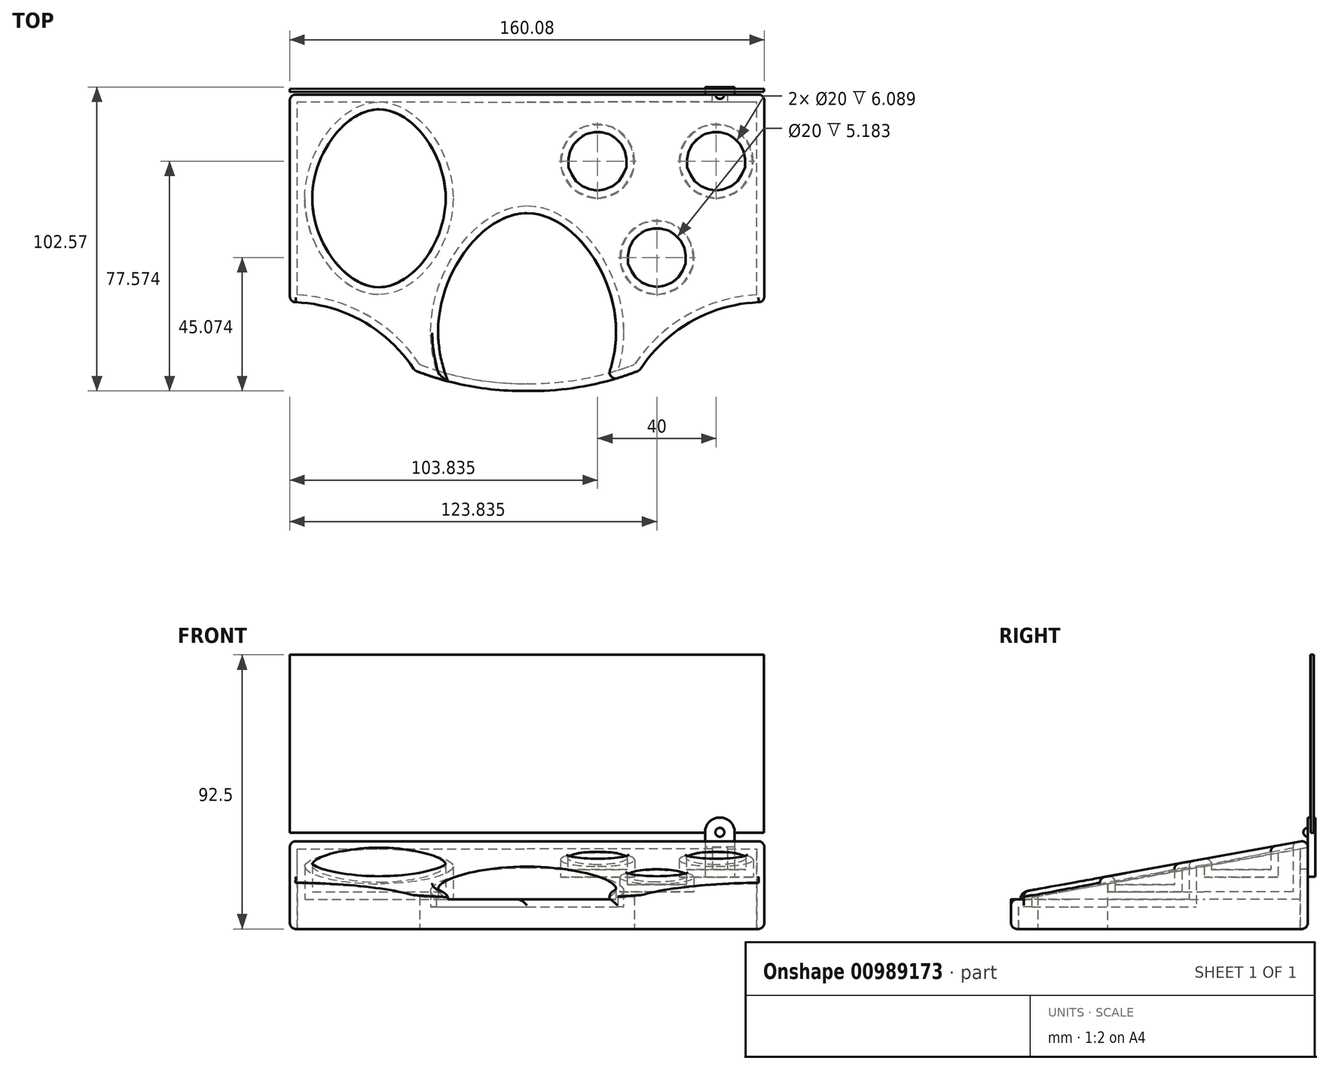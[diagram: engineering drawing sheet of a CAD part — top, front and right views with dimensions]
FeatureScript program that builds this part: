
annotation { "Feature Type Name" : "Feature", "Feature Type Description" : "" }
export const myFeature = defineFeature(function(context is Context, id is Id, definition is map)
    precondition{}
    {
        {
            var Q0;
            Q0=qCreatedBy(makeId("Top.planeOp"),FACE);
            var sketch = newSketch(context, id + "F0", { "sketchPlane" : qUnion([Q0])});
            skLineSegment(sketch, "E0.left", {"start": v(-80, 30) * mm, "end": v(-80, 100.06) * mm});
            skLineSegment(sketch, "E1", {"start": v(0, 0) * mm, "end": v(0, 30) * mm});
            skArc(sketch, "E2", {"start": v(-37.87, 6.93) * mm, "mid": v(-19.27, 1.63) * mm, "end": v(0, 0) * mm});
            skArc(sketch, "E3", {"start": v(-37.87, 6.93) * mm, "mid": v(-55.99, 23.86) * mm, "end": v(-80, 30) * mm});
            skLineSegment(sketch, "E4", {"start": v(0, 0) * mm, "end": v(0, 100) * mm});
            skLineSegment(sketch, "E5", {"start": v(-80, 100.06) * mm, "end": v(0, 100) * mm});
            skLineSegment(sketch, "E6.MirrorCS", {"start": v(80, 100.06) * mm, "end": v(0, 100) * mm});
            skLineSegment(sketch, "E7.MirrorCS", {"start": v(80, 30) * mm, "end": v(80, 100.06) * mm});
            skArc(sketch, "E8.MirrorCS", {"start": v(37.87, 6.93) * mm, "mid": v(55.99, 23.86) * mm, "end": v(80, 30) * mm});
            skArc(sketch, "E9.MirrorCS", {"start": v(37.87, 6.93) * mm, "mid": v(19.27, 1.63) * mm, "end": v(0, 0) * mm});
            skSolve(sketch);
        }
        {
            var Q0;
            Q0=makeQuery(id+"F0.imprint","IMPRINT",FACE,{"disambiguationData":[TD([[makeQuery(id+"F0.imprint","IMPRINT",EDGE,{"derivedFrom":sQuery(id+"F0.wireOp",EDGE,"E0.left")}),-1.0]])]});
            var Q1;
            {var subQ0=sQuery(id+"F0.wireOp",EDGE,"E6.MirrorCS");Q1=makeQuery(id+"F0.imprint","IMPRINT",FACE,{"disambiguationData":[TD([[makeQuery(id+"F0.imprint","IMPRINT",EDGE,{"derivedFrom":subQ0}),1.0]])]});}
            extrude(context, id + "F1", {"entities" : qUnion([Q0, Q1]), "depth" : 30 * mm, "offsetDistance" : 25 * mm});
        }
        {
            var Q0;
            Q0=makeQuery(id+"F1.opExtrude","SWEPT_FACE",FACE,{"disambiguationData":[OSD([sQuery(id+"F0.wireOp",EDGE,"E7.MirrorCS")])]});
            var sketch = newSketch(context, id + "F2", { "sketchPlane" : qUnion([Q0])});
            skLineSegment(sketch, "E10", {"start": v(0, 0) * mm, "end": v(-10, 0) * mm});
            skLineSegment(sketch, "E11", {"start": v(-10, 0) * mm, "end": v(-10, 10) * mm});
            skLineSegment(sketch, "E12", {"start": v(-10, 10) * mm, "end": v(-10, 30) * mm});
            skLineSegment(sketch, "E13", {"start": v(-10, 30) * mm, "end": v(100.06, 30) * mm});
            skLineSegment(sketch, "E14", {"start": v(100.06, 30) * mm, "end": v(-10, 10) * mm});
            skSolve(sketch);
        }
        {
            var Q0;
            Q0 = qSketchRegion(id + "F2", true);
            extrude(context, id + "F3", {"entities" : qUnion([Q0]), "operationType" : NewBodyOperationType.REMOVE, "endBound" : BoundingType.THROUGH_ALL, "oppositeDirection" : true, "depth" : 25 * mm, "offsetDistance" : 25 * mm});
        }
        {
            var Q0;
            Q0=qCreatedBy(makeId("Right.planeOp"),FACE);
            var sketch = newSketch(context, id + "F4", { "sketchPlane" : qUnion([Q0])});
            skLineSegment(sketch, "E15", {"start": v(0, 0) * mm, "end": v(0, 10) * mm});
            skLineSegment(sketch, "E16", {"start": v(0, 10) * mm, "end": v(40, 10) * mm});
            skLineSegment(sketch, "E17", {"start": v(40, 10) * mm, "end": v(40, 30) * mm});
            skLineSegment(sketch, "E18", {"start": v(40, 30) * mm, "end": v(0, 30) * mm});
            skLineSegment(sketch, "E19", {"start": v(0, 30) * mm, "end": v(0, 10) * mm});
            skLineSegment(sketch, "E20", {"start": v(0, 30) * mm, "end": v(-10, 30) * mm});
            skLineSegment(sketch, "E21", {"start": v(-10, 30) * mm, "end": v(-10, 10) * mm});
            skLineSegment(sketch, "E22", {"start": v(-10, 10) * mm, "end": v(0, 10) * mm});
            skSolve(sketch);
        }
        {
            var Q0;
            Q0 = qSketchRegion(id + "F4", true);
            extrude(context, id + "F5", {"entities" : qUnion([Q0]), "operationType" : NewBodyOperationType.REMOVE, "depth" : 10 * mm, "offsetDistance" : 25 * mm, "hasSecondDirection" : true, "secondDirectionOppositeDirection" : true, "secondDirectionDepth" : 10 * mm});
        }
        {
            var Q0;
            Q0=makeQuery(id+"F5.boolean.opBoolean","COPY",FACE,{"derivedFrom":makeQuery(id+"F5.opExtrude","SWEPT_FACE",FACE,{"disambiguationData":[OSD([sQuery(id+"F4.wireOp",EDGE,"E16"),sQuery(id+"F4.wireOp",EDGE,"E22")])]})});
            var sketch = newSketch(context, id + "F6", { "sketchPlane" : qUnion([Q0])});
            skLineSegment(sketch, "E23", {"start": v(0, 0) * mm, "end": v(0, 60) * mm});
            skLineSegment(sketch, "E24", {"start": v(0, 60) * mm, "end": v(0, -20) * mm});
            skLineSegment(sketch, "E25", {"start": v(0, 20) * mm, "end": v(-30, 20) * mm});
            skLineSegment(sketch, "E26", {"start": v(0, 20) * mm, "end": v(30, 20) * mm});
            skFitSpline(sketch, "E27", {"points": [v(-30, 20) * mm, v(0, 60) * mm, v(30, 20) * mm, v(0, -20) * mm, v(-30, 20) * mm]});
            skSolve(sketch);
        }
        {
            var Q0;
            Q0 = qSketchRegion(id + "F6", true);
            extrude(context, id + "F7", {"entities" : qUnion([Q0]), "operationType" : NewBodyOperationType.REMOVE, "endBound" : BoundingType.THROUGH_ALL, "depth" : 25 * mm, "offsetDistance" : 25 * mm});
        }
        {
            var Q0;
            Q0=makeQuery(id+"F7.boolean.opBoolean","MERGE",FACE,{"derivedFrom":[makeQuery(id+"F5.boolean.opBoolean","COPY",FACE,{"derivedFrom":makeQuery(id+"F5.opExtrude","SWEPT_FACE",FACE,{"disambiguationData":[OSD([sQuery(id+"F4.wireOp",EDGE,"E16"),sQuery(id+"F4.wireOp",EDGE,"E22")])]})})],"fromTools":[makeQuery(id+"F7.opExtrude","CAP_FACE",FACE,{"disambiguationData":[OSD([sQuery(id+"F6.wireOp",EDGE,"E27")])],"isStart":true})]});
            var sketch = newSketch(context, id + "F8", { "sketchPlane" : qUnion([Q0])});
            skLineSegment(sketch, "E28", {"start": v(0, 0) * mm, "end": v(1.26, 100.06) * mm});
            skLineSegment(sketch, "E29", {"start": v(1.26, 100.06) * mm, "end": v(81.26, 100.06) * mm});
            skLineSegment(sketch, "E30", {"start": v(41.26, 100.06) * mm, "end": v(43.76, 100.06) * mm});
            skLineSegment(sketch, "E31", {"start": v(43.76, 100.06) * mm, "end": v(43.76, 45.06) * mm});
            skLineSegment(sketch, "E32", {"start": v(43.76, 45.06) * mm, "end": v(43.76, 65.06) * mm});
            skCircle(sketch, "E33", {"center": v(23.76, 77.56) * mm, "radius": 10 * mm});
            skCircle(sketch, "E34", {"center": v(63.76, 77.56) * mm, "radius": 10 * mm});
            skCircle(sketch, "E35", {"center": v(43.76, 45.06) * mm, "radius": 10 * mm});
            skLineSegment(sketch, "E36", {"start": v(63.76, 77.56) * mm, "end": v(23.76, 77.56) * mm});
            skLineSegment(sketch, "E37", {"start": v(43.76, 77.56) * mm, "end": v(43.76, 45.06) * mm});
            skLineSegment(sketch, "E38", {"start": v(63.76, 77.56) * mm, "end": v(43.76, 77.56) * mm});
            skLineSegment(sketch, "E39", {"start": v(23.76, 77.56) * mm, "end": v(43.76, 77.56) * mm});
            skSolve(sketch);
        }
        {
            var Q0;
            Q0 = qSketchRegion(id + "F8", true);
            extrude(context, id + "F9", {"entities" : qUnion([Q0]), "operationType" : NewBodyOperationType.REMOVE, "endBound" : BoundingType.THROUGH_ALL, "depth" : 25 * mm, "offsetDistance" : 25 * mm});
        }
        {
            var Q0;
            Q0=makeQuery(id+"F7.boolean.opBoolean","MERGE",FACE,{"derivedFrom":[makeQuery(id+"F5.boolean.opBoolean","COPY",FACE,{"derivedFrom":makeQuery(id+"F5.opExtrude","SWEPT_FACE",FACE,{"disambiguationData":[OSD([sQuery(id+"F4.wireOp",EDGE,"E16"),sQuery(id+"F4.wireOp",EDGE,"E22")])]})})],"fromTools":[makeQuery(id+"F7.opExtrude","CAP_FACE",FACE,{"disambiguationData":[OSD([sQuery(id+"F6.wireOp",EDGE,"E27")])],"isStart":true})]});
            var sketch = newSketch(context, id + "F10", { "sketchPlane" : qUnion([Q0])});
            skLineSegment(sketch, "E40", {"start": v(-39.95, 100.02) * mm, "end": v(-49.95, 100.02) * mm});
            skLineSegment(sketch, "E41", {"start": v(-49.95, 100.02) * mm, "end": v(-49.95, 65.02) * mm});
            skLineSegment(sketch, "E42", {"start": v(-49.95, 65.02) * mm, "end": v(-49.95, 35.02) * mm});
            skLineSegment(sketch, "E43", {"start": v(-49.95, 65.02) * mm, "end": v(-49.95, 95.02) * mm});
            skLineSegment(sketch, "E44", {"start": v(-49.95, 65.02) * mm, "end": v(-72.45, 65.02) * mm});
            skLineSegment(sketch, "E45", {"start": v(-49.95, 65.02) * mm, "end": v(-27.45, 65.02) * mm});
            skFitSpline(sketch, "E46", {"points": [v(-49.95, 35.02) * mm, v(-72.45, 65.02) * mm, v(-49.95, 95.02) * mm, v(-27.45, 65.02) * mm, v(-49.95, 35.02) * mm]});
            skLineSegment(sketch, "E47", {"start": v(-39.95, 100.02) * mm, "end": v(0, 100) * mm});
            skSolve(sketch);
        }
        {
            var Q0;
            Q0 = qSketchRegion(id + "F10", true);
            var Q1;
            Q1=sQuery(id+"F10.wireOp",EDGE,"E46");
            extrude(context, id + "F11", {"entities" : qUnion([Q0]), "operationType" : NewBodyOperationType.REMOVE, "surfaceEntities" : qUnion([Q1]), "endBound" : BoundingType.THROUGH_ALL, "depth" : 25 * mm, "offsetDistance" : 25 * mm});
        }
        {
            var Q0;
            Q0=makeQuery(id+"F3.boolean.opBoolean","COPY",FACE,{"derivedFrom":makeQuery(id+"F3.opExtrude","SWEPT_FACE",FACE,{"disambiguationData":[OSD([sQuery(id+"F2.wireOp",EDGE,"E14")])]})});
            var Q1;
            Q1=makeQuery(id+"F1.opExtrude","CAP_FACE",FACE,{"disambiguationData":[OSD([sQuery(id+"F0.wireOp",EDGE,"E0.left"),sQuery(id+"F0.wireOp",EDGE,"E2"),sQuery(id+"F0.wireOp",EDGE,"E3"),sQuery(id+"F0.wireOp",EDGE,"E5"),sQuery(id+"F0.wireOp",EDGE,"E6.MirrorCS"),sQuery(id+"F0.wireOp",EDGE,"E7.MirrorCS"),sQuery(id+"F0.wireOp",EDGE,"E8.MirrorCS"),sQuery(id+"F0.wireOp",EDGE,"E9.MirrorCS")])],"isStart":true});
            var Q2;
            Q2=makeQuery(id+"F1.opExtrude","SWEPT_FACE",FACE,{"disambiguationData":[OSD([sQuery(id+"F0.wireOp",EDGE,"E6.MirrorCS")])]});
            var Q3;
            Q3=makeQuery(id+"F1.opExtrude","SWEPT_FACE",FACE,{"disambiguationData":[OSD([sQuery(id+"F0.wireOp",EDGE,"E5")])]});
            var Q4;
            Q4=makeQuery(id+"F1.opExtrude","SWEPT_FACE",FACE,{"disambiguationData":[OSD([sQuery(id+"F0.wireOp",EDGE,"E7.MirrorCS")])]});
            var Q5;
            Q5=makeQuery(id+"F1.opExtrude","SWEPT_FACE",FACE,{"disambiguationData":[OSD([sQuery(id+"F0.wireOp",EDGE,"E8.MirrorCS")])]});
            var Q6;
            Q6=makeQuery(id+"F1.opExtrude","SWEPT_FACE",FACE,{"disambiguationData":[OSD([sQuery(id+"F0.wireOp",EDGE,"E9.MirrorCS")])]});
            var Q7;
            Q7=makeQuery(id+"F1.opExtrude","SWEPT_FACE",FACE,{"disambiguationData":[OSD([sQuery(id+"F0.wireOp",EDGE,"E0.left")])]});
            var Q8;
            Q8=makeQuery(id+"F1.opExtrude","SWEPT_FACE",FACE,{"disambiguationData":[OSD([sQuery(id+"F0.wireOp",EDGE,"E3")])]});
            fillet(context, id + "F12", {"entities" : qUnion([Q0, Q1, Q2, Q3, Q4, Q5, Q6, Q7, Q8]), "radius" : 2 * mm, "tangentPropagation" : true, "allowEdgeOverflow" : false});
        }
        {
            var Q0;
            Q0=makeQuery(id+"F1.opExtrude","SWEPT_FACE",FACE,{"disambiguationData":[OSD([sQuery(id+"F0.wireOp",EDGE,"E6.MirrorCS")])]});
            var sketch = newSketch(context, id + "F13", { "sketchPlane" : qUnion([Q0])});
            skLineSegment(sketch, "E48", {"start": v(-0.08, 27.6) * mm, "end": v(-65.08, 27.6) * mm});
            skLineSegment(sketch, "E49.bottom", {"start": v(-65.08, 37.6) * mm, "end": v(-65.08, 37.6) * mm});
            skLineSegment(sketch, "E49.top", {"start": v(-60.08, 17.6) * mm, "end": v(-70.08, 17.6) * mm});
            skLineSegment(sketch, "E49.left", {"start": v(-60.08, 32.6) * mm, "end": v(-60.08, 17.6) * mm});
            skLineSegment(sketch, "E49.right", {"start": v(-70.08, 32.6) * mm, "end": v(-70.08, 17.6) * mm});
            skPoint(sketch, "E49.middle", {"position": v(-65.08, 27.6) * mm});
            skPoint(sketch, "E50.visualSharp", {"position": v(-60.08, 37.6) * mm});
            skArc(sketch, "E50.filletArc", {"start": v(-60.08, 32.6) * mm, "mid": v(-61.55, 36.14) * mm, "end": v(-65.08, 37.6) * mm});
            skPoint(sketch, "E51.visualSharp", {"position": v(-70.08, 37.6) * mm});
            skArc(sketch, "E51.filletArc", {"start": v(-65.08, 37.6) * mm, "mid": v(-68.62, 36.14) * mm, "end": v(-70.08, 32.6) * mm});
            skSolve(sketch);
        }
        {
            var Q0;
            Q0 = qSketchRegion(id + "F13", true);
            extrude(context, id + "F14", {"entities" : qUnion([Q0]), "operationType" : NewBodyOperationType.ADD, "depth" : 2.5 * mm, "offsetDistance" : 25 * mm});
        }
        {
            var Q0;
            Q0=makeQuery(id+"F14.opExtrude","CAP_FACE",FACE,{"disambiguationData":[OSD([sQuery(id+"F13.wireOp",EDGE,"E49.top"),sQuery(id+"F13.wireOp",EDGE,"E49.left"),sQuery(id+"F13.wireOp",EDGE,"E49.right"),sQuery(id+"F13.wireOp",EDGE,"E50.filletArc"),sQuery(id+"F13.wireOp",EDGE,"E51.filletArc")])],"isStart":true});
            var sketch = newSketch(context, id + "F15", { "sketchPlane" : qUnion([Q0])});
            skArc(sketch, "E52", {"start": v(66.58, 32.6) * mm, "mid": v(65.08, 34.1) * mm, "end": v(63.58, 32.6) * mm});
            skLineSegment(sketch, "E53", {"start": v(66.58, 32.6) * mm, "end": v(63.58, 32.6) * mm});
            skSolve(sketch);
        }
        {
            var Q0;
            Q0 = qSketchRegion(id + "F15", true);
            var Q1;
            Q1=sQuery(id+"F15.wireOp",EDGE,"E53");
            revolve(context, id + "F16", {"operationType" : NewBodyOperationType.ADD, "surfaceOperationType" : NewSurfaceOperationType.NEW, "entities" : qUnion([Q0]), "axis" : qUnion([Q1]), "revolveType" : RevolveType.FULL});
        }
        {
            var Q0;
            Q0=makeQuery(id+"F14.opExtrude","CAP_FACE",FACE,{"disambiguationData":[OSD([sQuery(id+"F13.wireOp",EDGE,"E49.top"),sQuery(id+"F13.wireOp",EDGE,"E49.left"),sQuery(id+"F13.wireOp",EDGE,"E49.right"),sQuery(id+"F13.wireOp",EDGE,"E50.filletArc"),sQuery(id+"F13.wireOp",EDGE,"E51.filletArc")])],"isStart":false});
            cPlane(context, id + "F17", {"entities" : qUnion([Q0]), "cplaneType" : CPlaneType.OFFSET, "offset" : 1 * mm, "oppositeDirection" : true, "width" : 150 * mm, "height" : 150 * mm});
        }
        {
            var Q0;
            Q0=qCreatedBy(id+"F17.planeOp",FACE);
            var sketch = newSketch(context, id + "F18", { "sketchPlane" : qUnion([Q0])});
            skLineSegment(sketch, "E54", {"start": v(0, 0) * mm, "end": v(0, 32.5) * mm});
            skLineSegment(sketch, "E55", {"start": v(0, 32.5) * mm, "end": v(-80, 32.5) * mm});
            skLineSegment(sketch, "E56", {"start": v(-80, 32.5) * mm, "end": v(-80, 92.5) * mm});
            skLineSegment(sketch, "E57", {"start": v(-80, 92.5) * mm, "end": v(0, 92.5) * mm});
            skLineSegment(sketch, "E58", {"start": v(0, 92.5) * mm, "end": v(80, 92.5) * mm});
            skLineSegment(sketch, "E59", {"start": v(80, 92.5) * mm, "end": v(80, 32.5) * mm});
            skLineSegment(sketch, "E60", {"start": v(80, 32.5) * mm, "end": v(0, 32.5) * mm});
            skSolve(sketch);
        }
        {
            var Q0;
            Q0 = qSketchRegion(id + "F18", true);
            extrude(context, id + "F19", {"entities" : qUnion([Q0]), "operationType" : NewBodyOperationType.ADD, "depth" : 0.5 * mm, "offsetDistance" : 25 * mm, "hasSecondDirection" : true, "secondDirectionOppositeDirection" : true, "secondDirectionDepth" : 0.5 * mm});
        }
        {
            var Q0;
            Q0 = qSketchRegion(id + "F10", true);
            extrude(context, id + "F20", {"entities" : qUnion([Q0]), "operationType" : NewBodyOperationType.ADD, "depth" : 2.5 * mm, "offsetDistance" : 25 * mm});
        }
        {
            var Q0;
            Q0 = qSketchRegion(id + "F8", true);
            extrude(context, id + "F21", {"entities" : qUnion([Q0]), "operationType" : NewBodyOperationType.ADD, "depth" : 5 * mm, "offsetDistance" : 25 * mm});
        }
        {
            var Q0;
            Q0=makeQuery(id+"F21.opExtrude","CAP_FACE",FACE,{"disambiguationData":[OSD([sQuery(id+"F8.wireOp",EDGE,"E33")])],"isStart":false});
            var Q1;
            Q1=makeQuery(id+"F21.opExtrude","CAP_FACE",FACE,{"disambiguationData":[OSD([sQuery(id+"F8.wireOp",EDGE,"E34")])],"isStart":false});
            extrude(context, id + "F22", {"entities" : qUnion([Q0, Q1]), "operationType" : NewBodyOperationType.ADD, "depth" : 5 * mm, "offsetDistance" : 25 * mm});
        }
        {
            var Q0;
            Q0=makeQuery(id+"F1.opExtrude","CAP_FACE",FACE,{"disambiguationData":[OSD([sQuery(id+"F0.wireOp",EDGE,"E0.left"),sQuery(id+"F0.wireOp",EDGE,"E2"),sQuery(id+"F0.wireOp",EDGE,"E3"),sQuery(id+"F0.wireOp",EDGE,"E5"),sQuery(id+"F0.wireOp",EDGE,"E6.MirrorCS"),sQuery(id+"F0.wireOp",EDGE,"E7.MirrorCS"),sQuery(id+"F0.wireOp",EDGE,"E8.MirrorCS"),sQuery(id+"F0.wireOp",EDGE,"E9.MirrorCS")])],"isStart":true});
            shell(context, id + "F23", {"entities" : qUnion([Q0]), "thickness" : 2.5 * mm});
        }
    });
